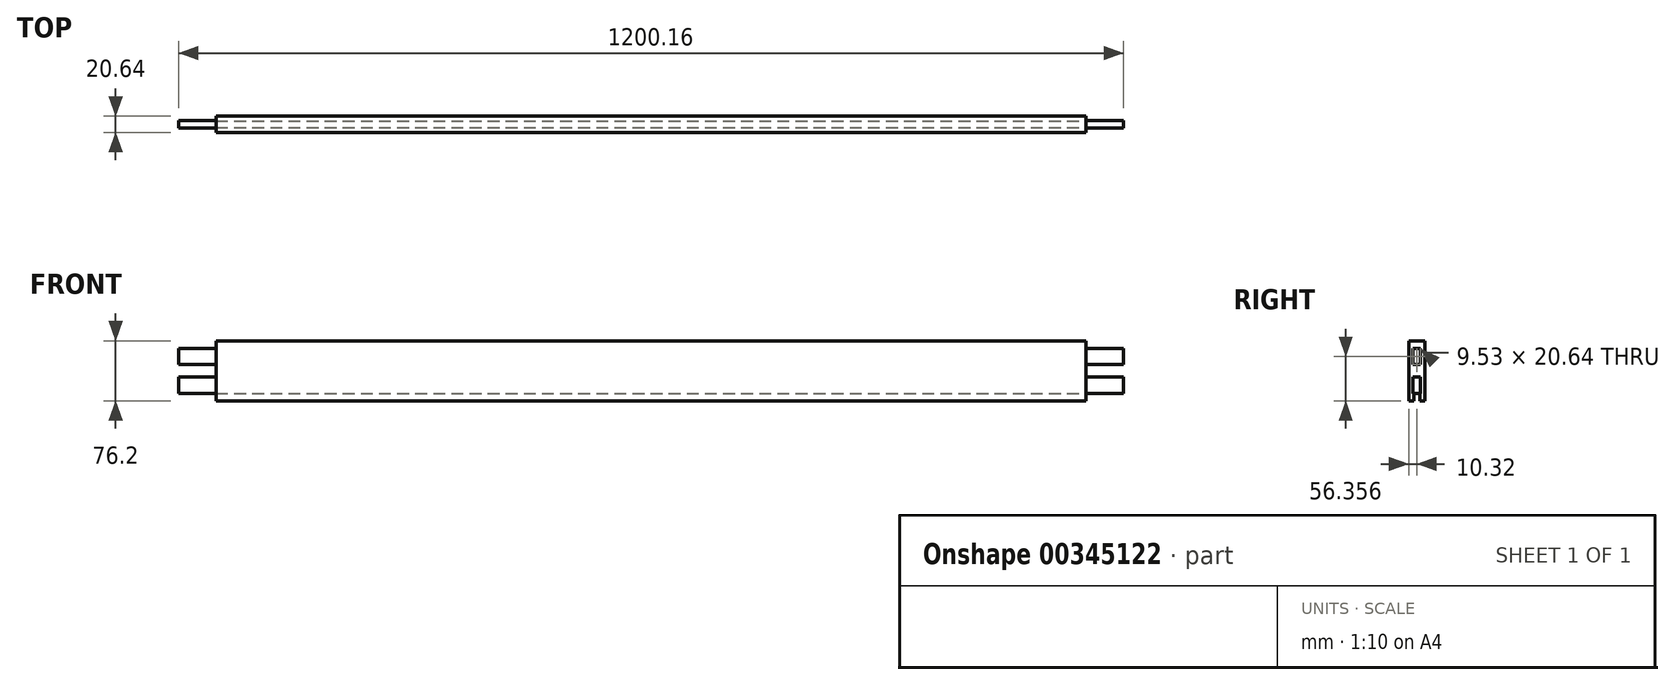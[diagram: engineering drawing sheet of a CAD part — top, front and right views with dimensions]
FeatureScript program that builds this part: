
annotation { "Feature Type Name" : "Feature", "Feature Type Description" : "" }
export const myFeature = defineFeature(function(context is Context, id is Id, definition is map)
    precondition{}
    {
        {
            var Q0;
            Q0=qCreatedBy(makeId("Front.planeOp"),FACE);
            var sketch = newSketch(context, id + "F0", { "sketchPlane" : qUnion([Q0])});
            skLineSegment(sketch, "E0.bottom", {"start": v(-552.45, -38.1) * mm, "end": v(552.45, -38.1) * mm});
            skLineSegment(sketch, "E0.top", {"start": v(-552.45, 38.1) * mm, "end": v(552.45, 38.1) * mm});
            skLineSegment(sketch, "E0.left", {"start": v(-552.45, -38.1) * mm, "end": v(-552.45, 38.1) * mm});
            skLineSegment(sketch, "E0.right", {"start": v(552.45, -38.1) * mm, "end": v(552.45, 38.1) * mm});
            skPoint(sketch, "E0.middle", {"position": v(0, 0) * mm});
            skSolve(sketch);
        }
        {
            var Q0;
            Q0=makeQuery(id+"F0.imprint","IMPRINT",FACE,{"disambiguationData":[TD([[makeQuery(id+"F0.imprint","IMPRINT",EDGE,{"derivedFrom":sQuery(id+"F0.wireOp",EDGE,"E0.bottom")}),1.0]])]});
            extrude(context, id + "F1", {"entities" : qUnion([Q0]), "endBound" : BoundingType.SYMMETRIC, "depth" : 20.64 * mm});
        }
        {
            var Q0;
            Q0=makeQuery(id+"F1.opExtrude","SWEPT_FACE",FACE,{"disambiguationData":[OSD([sQuery(id+"F0.wireOp",EDGE,"E0.right")])]});
            var sketch = newSketch(context, id + "F2", { "sketchPlane" : qUnion([Q0])});
            skLineSegment(sketch, "E1.bottom", {"start": v(-4.76, 7.94) * mm, "end": v(4.76, 7.94) * mm});
            skLineSegment(sketch, "E1.top", {"start": v(-4.76, 28.57) * mm, "end": v(4.76, 28.57) * mm});
            skLineSegment(sketch, "E1.left", {"start": v(-4.76, 7.94) * mm, "end": v(-4.76, 28.57) * mm});
            skLineSegment(sketch, "E1.right", {"start": v(4.76, 7.94) * mm, "end": v(4.76, 28.57) * mm});
            skPoint(sketch, "E1.middle", {"position": v(0, 18.26) * mm});
            skPoint(sketch, "E1.middle.positionSnap0", {"position": v(0, 38.1) * mm});
            skPoint(sketch, "E1.centerSnap0", {"position": v(0, 38.1) * mm});
            skLineSegment(sketch, "E2", {"start": v(-17.93, 0) * mm, "end": v(21.43, 0) * mm, "construction": true});
            skLineSegment(sketch, "E3.MirrorCS", {"start": v(-4.76, -28.58) * mm, "end": v(4.76, -28.58) * mm});
            skLineSegment(sketch, "E4.MirrorCS", {"start": v(-4.76, -7.94) * mm, "end": v(-4.76, -28.58) * mm});
            skLineSegment(sketch, "E5.MirrorCS", {"start": v(4.76, -7.94) * mm, "end": v(4.76, -28.58) * mm});
            skLineSegment(sketch, "E6.MirrorCS", {"start": v(-4.76, -7.94) * mm, "end": v(4.76, -7.94) * mm});
            skSolve(sketch);
        }
        {
            var Q0;
            Q0=makeQuery(id+"F2.imprint","IMPRINT",FACE,{"disambiguationData":[TD([[makeQuery(id+"F2.imprint","IMPRINT",EDGE,{"derivedFrom":sQuery(id+"F2.wireOp",EDGE,"E1.bottom")}),1.0]])]});
            var Q1;
            Q1=makeQuery(id+"F2.imprint","IMPRINT",FACE,{"disambiguationData":[TD([[makeQuery(id+"F2.imprint","IMPRINT",EDGE,{"derivedFrom":sQuery(id+"F2.wireOp",EDGE,"E3.MirrorCS")}),1.0]])]});
            extrude(context, id + "F3", {"entities" : qUnion([Q0, Q1]), "operationType" : NewBodyOperationType.ADD, "depth" : 47.62 * mm});
        }
        {
            var Q0;
            Q0=makeQuery(id+"F1.opExtrude","SWEPT_FACE",FACE,{"disambiguationData":[OSD([sQuery(id+"F0.wireOp",EDGE,"E0.left")])]});
            var sketch = newSketch(context, id + "F4", { "sketchPlane" : qUnion([Q0])});
            skLineSegment(sketch, "E7.bottom", {"start": v(4.76, 7.94) * mm, "end": v(-4.76, 7.94) * mm});
            skLineSegment(sketch, "E7.top", {"start": v(4.76, 28.58) * mm, "end": v(-4.76, 28.58) * mm});
            skLineSegment(sketch, "E7.left", {"start": v(4.76, 7.94) * mm, "end": v(4.76, 28.58) * mm});
            skLineSegment(sketch, "E7.right", {"start": v(-4.76, 7.94) * mm, "end": v(-4.76, 28.58) * mm});
            skPoint(sketch, "E7.middle", {"position": v(0, 18.26) * mm});
            skPoint(sketch, "E7.middle.positionSnap0", {"position": v(0, 38.1) * mm});
            skPoint(sketch, "E7.centerSnap0", {"position": v(0, 38.1) * mm});
            skLineSegment(sketch, "E8", {"start": v(-11.2, 0) * mm, "end": v(13.7, 0) * mm, "construction": true});
            skLineSegment(sketch, "E9.MirrorCS", {"start": v(-4.76, -7.94) * mm, "end": v(-4.76, -28.57) * mm});
            skLineSegment(sketch, "E10.MirrorCS", {"start": v(4.76, -28.57) * mm, "end": v(-4.76, -28.57) * mm});
            skLineSegment(sketch, "E11.MirrorCS", {"start": v(4.76, -7.94) * mm, "end": v(4.76, -28.57) * mm});
            skLineSegment(sketch, "E12.MirrorCS", {"start": v(4.76, -7.94) * mm, "end": v(-4.76, -7.94) * mm});
            skSolve(sketch);
        }
        {
            var Q0;
            Q0=makeQuery(id+"F4.imprint","IMPRINT",FACE,{"disambiguationData":[TD([[makeQuery(id+"F4.imprint","IMPRINT",EDGE,{"derivedFrom":sQuery(id+"F4.wireOp",EDGE,"E9.MirrorCS")}),1.0]])]});
            var Q1;
            Q1=makeQuery(id+"F4.imprint","IMPRINT",FACE,{"disambiguationData":[TD([[makeQuery(id+"F4.imprint","IMPRINT",EDGE,{"derivedFrom":sQuery(id+"F4.wireOp",EDGE,"E7.bottom")}),-1.0]])]});
            extrude(context, id + "F5", {"entities" : qUnion([Q0, Q1]), "operationType" : NewBodyOperationType.ADD, "depth" : 47.62 * mm});
        }
        {
            var Q0;
            Q0=makeQuery(id+"F1.opExtrude","SWEPT_FACE",FACE,{"disambiguationData":[OSD([sQuery(id+"F0.wireOp",EDGE,"E0.bottom")])]});
            var sketch = newSketch(context, id + "F6", { "sketchPlane" : qUnion([Q0])});
            skLineSegment(sketch, "E13.bottom", {"start": v(-552.45, 3.97) * mm, "end": v(552.45, 3.97) * mm});
            skLineSegment(sketch, "E13.top", {"start": v(-552.45, -3.97) * mm, "end": v(552.45, -3.97) * mm});
            skLineSegment(sketch, "E13.left", {"start": v(-552.45, 3.97) * mm, "end": v(-552.45, -3.97) * mm});
            skLineSegment(sketch, "E13.right", {"start": v(552.45, 3.97) * mm, "end": v(552.45, -3.97) * mm});
            skPoint(sketch, "E13.middle", {"position": v(0, 0) * mm});
            skSolve(sketch);
        }
        {
            var Q0;
            Q0 = qSketchRegion(id + "F6", true);
            extrude(context, id + "F7", {"entities" : qUnion([Q0]), "operationType" : NewBodyOperationType.REMOVE, "oppositeDirection" : true, "depth" : 9.52 * mm});
        }
    });
